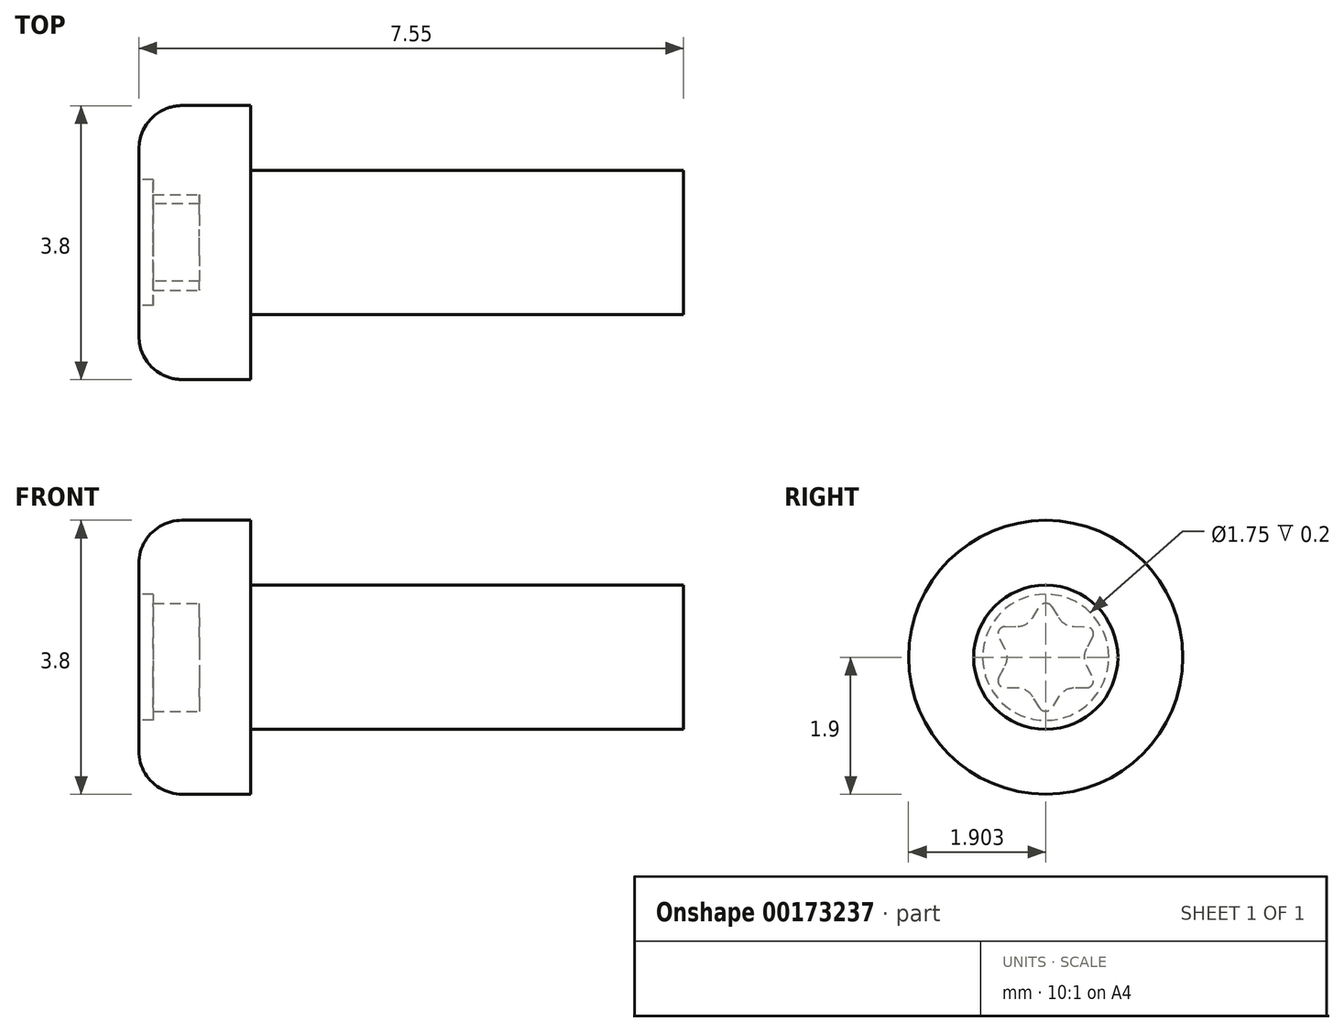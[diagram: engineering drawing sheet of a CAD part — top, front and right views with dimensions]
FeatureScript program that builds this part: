
annotation { "Feature Type Name" : "Feature", "Feature Type Description" : "" }
export const myFeature = defineFeature(function(context is Context, id is Id, definition is map)
    precondition{}
    {
        {
            var Q0;
            Q0=qCreatedBy(makeId("Top.planeOp"),FACE);
            var sketch = newSketch(context, id + "F0", { "sketchPlane" : qUnion([Q0])});
            skLineSegment(sketch, "E0", {"start": v(6.6, 5.28) * mm, "end": v(6.6, 3.38) * mm});
            skLineSegment(sketch, "E1", {"start": v(5.05, 3.38) * mm, "end": v(5.05, 5.28) * mm});
            skLineSegment(sketch, "E2", {"start": v(5.05, 5.28) * mm, "end": v(6.6, 5.28) * mm});
            skLineSegment(sketch, "E3", {"start": v(6.6, 3.38) * mm, "end": v(5.05, 3.38) * mm});
            skSolve(sketch);
        }
        {
            var Q0;
            Q0=makeQuery(id+"F0.imprint","IMPRINT",FACE,{"disambiguationData":[TD([[makeQuery(id+"F0.imprint","IMPRINT",EDGE,{"derivedFrom":sQuery(id+"F0.wireOp",EDGE,"E0")}),-1.0]])]});
            var Q1;
            Q1=sQuery(id+"F0.wireOp",EDGE,"E3");
            revolve(context, id + "F1", {"entities" : qUnion([Q0]), "axis" : qUnion([Q1]), "revolveType" : RevolveType.FULL});
        }
        {
            var Q0;
            Q0=makeQuery(id+"F1.opRevolve","SWEPT_FACE",FACE,{"disambiguationData":[OSD([sQuery(id+"F0.wireOp",EDGE,"E1")])]});
            fillet(context, id + "F2", {"entities" : qUnion([Q0]), "radius" : 0.6 * mm, "tangentPropagation" : true, "allowEdgeOverflow" : false});
        }
        {
            var Q0;
            Q0=makeQuery(id+"F1.opRevolve","SWEPT_FACE",FACE,{"disambiguationData":[OSD([sQuery(id+"F0.wireOp",EDGE,"E1")])]});
            var sketch = newSketch(context, id + "F3", { "sketchPlane" : qUnion([Q0])});
            skCircle(sketch, "E4", {"center": v(-3.38, 0) * mm, "radius": 0.88 * mm});
            skSolve(sketch);
        }
        {
            var Q0;
            Q0 = qSketchRegion(id + "F3", true);
            extrude(context, id + "F4", {"entities" : qUnion([Q0]), "operationType" : NewBodyOperationType.REMOVE, "oppositeDirection" : true, "depth" : 0.2 * mm});
        }
        {
            var Q0;
            Q0=makeQuery(id+"F1.opRevolve","SWEPT_FACE",FACE,{"disambiguationData":[OSD([sQuery(id+"F0.wireOp",EDGE,"E0")])]});
            var sketch = newSketch(context, id + "F5", { "sketchPlane" : qUnion([Q0])});
            skCircle(sketch, "E5", {"center": v(3.38, 0) * mm, "radius": 1 * mm});
            skSolve(sketch);
        }
        {
            var Q0;
            Q0=makeQuery(id+"F5.imprint","IMPRINT",FACE,{"disambiguationData":[TD([[makeQuery(id+"F5.imprint","IMPRINT",EDGE,{"derivedFrom":sQuery(id+"F5.wireOp",EDGE,"E5")}),1.0]])]});
            extrude(context, id + "F6", {"entities" : qUnion([Q0]), "operationType" : NewBodyOperationType.ADD, "depth" : 6 * mm});
        }
        {
            var Q0;
            Q0=makeQuery(id+"F4.boolean.opBoolean","COPY",FACE,{"derivedFrom":makeQuery(id+"F4.opExtrude","CAP_FACE",FACE,{"disambiguationData":[OSD([sQuery(id+"F3.wireOp",EDGE,"E4")])],"isStart":false})});
            var sketch = newSketch(context, id + "F7", { "sketchPlane" : qUnion([Q0])});
            skPoint(sketch, "E6.center", {"position": v(-3.38, 0) * mm});
            skLineSegment(sketch, "E7", {"start": v(-3.38, 0.84) * mm, "end": v(-3.63, 0.43) * mm});
            skLineSegment(sketch, "E8", {"start": v(-3.63, 0.43) * mm, "end": v(-4.11, 0.42) * mm});
            skLineSegment(sketch, "E9", {"start": v(-4.11, 0.42) * mm, "end": v(-3.88, 0) * mm});
            skLineSegment(sketch, "E10", {"start": v(-3.88, 0) * mm, "end": v(-4.11, -0.42) * mm});
            skLineSegment(sketch, "E11", {"start": v(-4.11, -0.42) * mm, "end": v(-3.63, -0.43) * mm});
            skLineSegment(sketch, "E12", {"start": v(-3.63, -0.43) * mm, "end": v(-3.38, -0.84) * mm});
            skLineSegment(sketch, "E13", {"start": v(-3.38, -0.84) * mm, "end": v(-3.13, -0.43) * mm});
            skLineSegment(sketch, "E14", {"start": v(-3.13, -0.43) * mm, "end": v(-2.66, -0.42) * mm});
            skLineSegment(sketch, "E15", {"start": v(-2.66, -0.42) * mm, "end": v(-2.88, 0) * mm});
            skLineSegment(sketch, "E16", {"start": v(-2.88, 0) * mm, "end": v(-2.66, 0.42) * mm});
            skLineSegment(sketch, "E17", {"start": v(-2.66, 0.42) * mm, "end": v(-3.13, 0.43) * mm});
            skLineSegment(sketch, "E18", {"start": v(-3.13, 0.43) * mm, "end": v(-3.38, 0.84) * mm});
            skSolve(sketch);
        }
        {
            var Q0;
            Q0 = qSketchRegion(id + "F7", true);
            extrude(context, id + "F8", {"entities" : qUnion([Q0]), "operationType" : NewBodyOperationType.REMOVE, "oppositeDirection" : true, "depth" : 0.64 * mm});
        }
        {
            var Q0;
            Q0=makeQuery(id+"F8.boolean.opBoolean","COPY",EDGE,{"derivedFrom":makeQuery(id+"F8.opExtrude","SWEPT_EDGE",EDGE,{"disambiguationData":[OSD([sQuery(id+"F7.wireOp",EDGE,"E7"),sQuery(id+"F7.wireOp",EDGE,"E18")])]})});
            var Q1;
            Q1=makeQuery(id+"F8.boolean.opBoolean","COPY",EDGE,{"derivedFrom":makeQuery(id+"F8.opExtrude","SWEPT_EDGE",EDGE,{"disambiguationData":[OSD([sQuery(id+"F7.wireOp",EDGE,"E8"),sQuery(id+"F7.wireOp",EDGE,"E9")])]})});
            var Q2;
            Q2=makeQuery(id+"F8.boolean.opBoolean","COPY",EDGE,{"derivedFrom":makeQuery(id+"F8.opExtrude","SWEPT_EDGE",EDGE,{"disambiguationData":[OSD([sQuery(id+"F7.wireOp",EDGE,"E10"),sQuery(id+"F7.wireOp",EDGE,"E11")])]})});
            var Q3;
            Q3=makeQuery(id+"F8.boolean.opBoolean","COPY",EDGE,{"derivedFrom":makeQuery(id+"F8.opExtrude","SWEPT_EDGE",EDGE,{"disambiguationData":[OSD([sQuery(id+"F7.wireOp",EDGE,"E12"),sQuery(id+"F7.wireOp",EDGE,"E13")])]})});
            var Q4;
            Q4=makeQuery(id+"F8.boolean.opBoolean","COPY",EDGE,{"derivedFrom":makeQuery(id+"F8.opExtrude","SWEPT_EDGE",EDGE,{"disambiguationData":[OSD([sQuery(id+"F7.wireOp",EDGE,"E14"),sQuery(id+"F7.wireOp",EDGE,"E15")])]})});
            var Q5;
            Q5=makeQuery(id+"F8.boolean.opBoolean","COPY",EDGE,{"derivedFrom":makeQuery(id+"F8.opExtrude","SWEPT_EDGE",EDGE,{"disambiguationData":[OSD([sQuery(id+"F7.wireOp",EDGE,"E16"),sQuery(id+"F7.wireOp",EDGE,"E17")])]})});
            fillet(context, id + "F9", {"entities" : qUnion([Q0, Q1, Q2, Q3, Q4, Q5]), "radius" : 0.1 * mm, "tangentPropagation" : true, "allowEdgeOverflow" : false});
        }
        {
            var Q0;
            Q0=makeQuery(id+"F8.boolean.opBoolean","COPY",EDGE,{"derivedFrom":makeQuery(id+"F8.opExtrude","SWEPT_EDGE",EDGE,{"disambiguationData":[OSD([sQuery(id+"F7.wireOp",EDGE,"E7"),sQuery(id+"F7.wireOp",EDGE,"E8")])]})});
            var Q1;
            Q1=makeQuery(id+"F8.boolean.opBoolean","COPY",EDGE,{"derivedFrom":makeQuery(id+"F8.opExtrude","SWEPT_EDGE",EDGE,{"disambiguationData":[OSD([sQuery(id+"F7.wireOp",EDGE,"E9"),sQuery(id+"F7.wireOp",EDGE,"E10")])]})});
            var Q2;
            Q2=makeQuery(id+"F8.boolean.opBoolean","COPY",EDGE,{"derivedFrom":makeQuery(id+"F8.opExtrude","SWEPT_EDGE",EDGE,{"disambiguationData":[OSD([sQuery(id+"F7.wireOp",EDGE,"E11"),sQuery(id+"F7.wireOp",EDGE,"E12")])]})});
            var Q3;
            Q3=makeQuery(id+"F8.boolean.opBoolean","COPY",EDGE,{"derivedFrom":makeQuery(id+"F8.opExtrude","SWEPT_EDGE",EDGE,{"disambiguationData":[OSD([sQuery(id+"F7.wireOp",EDGE,"E17"),sQuery(id+"F7.wireOp",EDGE,"E18")])]})});
            var Q4;
            Q4=makeQuery(id+"F8.boolean.opBoolean","COPY",EDGE,{"derivedFrom":makeQuery(id+"F8.opExtrude","SWEPT_EDGE",EDGE,{"disambiguationData":[OSD([sQuery(id+"F7.wireOp",EDGE,"E13"),sQuery(id+"F7.wireOp",EDGE,"E14")])]})});
            var Q5;
            Q5=makeQuery(id+"F8.boolean.opBoolean","COPY",EDGE,{"derivedFrom":makeQuery(id+"F8.opExtrude","SWEPT_EDGE",EDGE,{"disambiguationData":[OSD([sQuery(id+"F7.wireOp",EDGE,"E15"),sQuery(id+"F7.wireOp",EDGE,"E16")])]})});
            fillet(context, id + "F10", {"entities" : qUnion([Q0, Q1, Q2, Q3, Q4, Q5]), "radius" : 0.25 * mm, "tangentPropagation" : true, "allowEdgeOverflow" : false});
        }
    });
